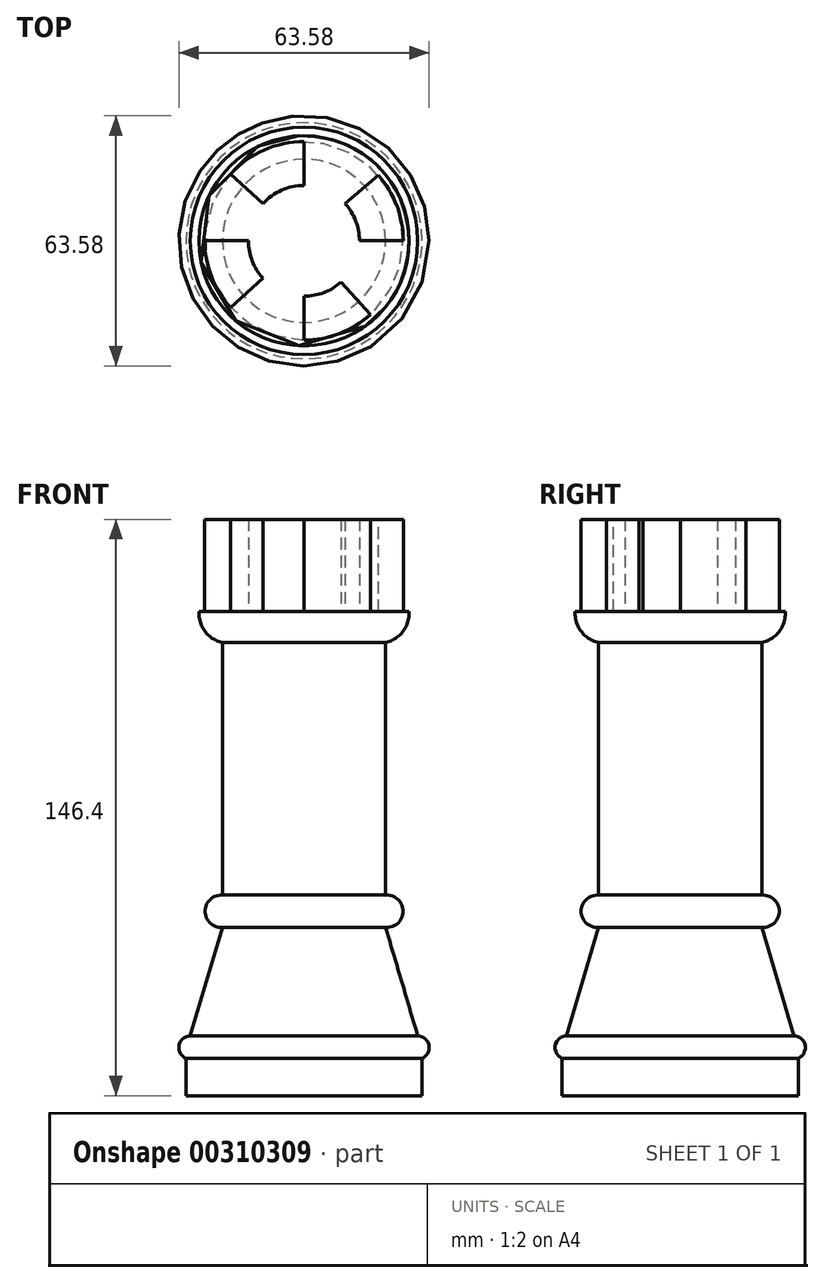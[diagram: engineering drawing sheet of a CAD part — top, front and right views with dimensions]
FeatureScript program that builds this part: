
annotation { "Feature Type Name" : "Feature", "Feature Type Description" : "" }
export const myFeature = defineFeature(function(context is Context, id is Id, definition is map)
    precondition{}
    {
        {
            var Q0;
            Q0=qCreatedBy(makeId("Front.planeOp"),FACE);
            var sketch = newSketch(context, id + "F0", { "sketchPlane" : qUnion([Q0])});
            skLineSegment(sketch, "E0", {"start": v(25.22, 52.85) * mm, "end": v(26.69, 52.85) * mm});
            skArc(sketch, "E1", {"start": v(20.73, 44.91) * mm, "mid": v(25.16, 47.8) * mm, "end": v(26.69, 52.85) * mm});
            skLineSegment(sketch, "E2", {"start": v(20.73, 44.91) * mm, "end": v(20.73, -19.25) * mm});
            skLineSegment(sketch, "E3", {"start": v(20.73, -27.41) * mm, "end": v(28.9, -54.97) * mm});
            skLineSegment(sketch, "E4", {"start": v(0, -70.19) * mm, "end": v(30, -70.19) * mm});
            skLineSegment(sketch, "E5", {"start": v(30, -70.19) * mm, "end": v(30, -60.7) * mm});
            skArc(sketch, "E6", {"start": v(20.73, -27.41) * mm, "mid": v(25.16, -23.33) * mm, "end": v(20.73, -19.25) * mm});
            skArc(sketch, "E7", {"start": v(30, -60.7) * mm, "mid": v(31.74, -57.4) * mm, "end": v(28.9, -54.97) * mm});
            skLineSegment(sketch, "E8", {"start": v(0, 52.85) * mm, "end": v(0, -70.19) * mm});
            skLineSegment(sketch, "E9", {"start": v(0, 52.85) * mm, "end": v(0, 76.2) * mm});
            skLineSegment(sketch, "E10", {"start": v(25.22, 52.85) * mm, "end": v(25.22, 76.2) * mm});
            skLineSegment(sketch, "E11", {"start": v(25.22, 76.2) * mm, "end": v(0, 76.2) * mm});
            skSolve(sketch);
        }
        {
            var Q0;
            Q0=makeQuery(id+"F0.imprint","IMPRINT",FACE,{"disambiguationData":[TD([[makeQuery(id+"F0.imprint","IMPRINT",EDGE,{"derivedFrom":sQuery(id+"F0.wireOp",EDGE,"E0")}),-1.0]])]});
            var Q1;
            Q1=sQuery(id+"F0.wireOp",EDGE,"E8");
            revolve(context, id + "F1", {"entities" : qUnion([Q0]), "axis" : qUnion([Q1]), "revolveType" : RevolveType.FULL});
        }
        {
            var Q0;
            Q0=makeQuery(id+"F1.opRevolve","SWEPT_FACE",FACE,{"disambiguationData":[OSD([sQuery(id+"F0.wireOp",EDGE,"E0")])]});
            var sketch = newSketch(context, id + "F2", { "sketchPlane" : qUnion([Q0])});
            skArc(sketch, "E12", {"start": v(-14.09, 0) * mm, "mid": v(-13.15, -5.07) * mm, "end": v(-10.44, -9.45) * mm});
            skLineSegment(sketch, "E13", {"start": v(14.09, 0) * mm, "end": v(25.35, 0) * mm});
            skLineSegment(sketch, "E14", {"start": v(0, 14.09) * mm, "end": v(0, 25.35) * mm});
            skLineSegment(sketch, "E15", {"start": v(-25.35, 0) * mm, "end": v(-14.09, 0) * mm});
            skLineSegment(sketch, "E16", {"start": v(0, -25.35) * mm, "end": v(0, -14.09) * mm});
            skLineSegment(sketch, "E17", {"start": v(-10.44, -9.45) * mm, "end": v(-18.8, -17) * mm});
            skLineSegment(sketch, "E18", {"start": v(9.44, -10.45) * mm, "end": v(16.93, -18.87) * mm});
            skLineSegment(sketch, "E19", {"start": v(-10.46, 9.44) * mm, "end": v(-18.72, 17.1) * mm});
            skLineSegment(sketch, "E20", {"start": v(10.46, 9.44) * mm, "end": v(18.98, 16.8) * mm});
            skPoint(sketch, "E21", {"position": v(-10.46, 9.44) * mm});
            skPoint(sketch, "E22", {"position": v(0, 14.09) * mm});
            skPoint(sketch, "E23", {"position": v(10.46, 9.44) * mm});
            skPoint(sketch, "E24", {"position": v(9.44, -10.45) * mm});
            skPoint(sketch, "E25", {"position": v(14.09, 0) * mm});
            skPoint(sketch, "E26", {"position": v(0, -14.09) * mm});
            skPoint(sketch, "E27", {"position": v(-10.44, -9.45) * mm});
            skPoint(sketch, "E28", {"position": v(-14.09, 0) * mm});
            skArc(sketch, "E29.trimOffspring", {"start": v(0, -14.09) * mm, "mid": v(5.06, -13.15) * mm, "end": v(9.44, -10.45) * mm});
            skArc(sketch, "E30.trimOffspring", {"start": v(14.09, 0) * mm, "mid": v(13.15, 5.06) * mm, "end": v(10.46, 9.44) * mm});
            skArc(sketch, "E31.trimOffspring", {"start": v(0, 14.09) * mm, "mid": v(-5.72, 12.87) * mm, "end": v(-10.46, 9.44) * mm});
            skArc(sketch, "E32", {"start": v(-18.72, 17.1) * mm, "mid": v(-23.63, 9.17) * mm, "end": v(-25.35, 0) * mm});
            skArc(sketch, "E33.trimOffspring", {"start": v(-18.8, -17) * mm, "mid": v(-10.3, -23.17) * mm, "end": v(0, -25.35) * mm});
            skArc(sketch, "E34.trimOffspring", {"start": v(16.93, -18.87) * mm, "mid": v(23.15, -10.33) * mm, "end": v(25.35, 0) * mm});
            skArc(sketch, "E35.trimOffspring", {"start": v(18.98, 16.8) * mm, "mid": v(10.4, 23.11) * mm, "end": v(0, 25.35) * mm});
            skSolve(sketch);
        }
        {
            var Q0;
            Q0 = qSketchRegion(id + "F2", true);
            extrude(context, id + "F3", {"entities" : qUnion([Q0]), "operationType" : NewBodyOperationType.REMOVE, "depth" : 27.7 * mm});
        }
    });
